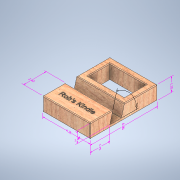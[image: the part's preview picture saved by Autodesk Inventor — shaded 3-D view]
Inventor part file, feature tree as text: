
AUTODESK INVENTOR PART (.ipt)
format: ipt  version: 2020.2 (Build 242310000, 310)  size: 403,456 bytes
history: native  units: in
note: dims shown in document units (in); Inventor stores cm internally (conversion verified against a paired STEP export)
features: other x8, extrude x4, sketch x4, fillet x2
ambient origin geometry x8: Origin, YZ Plane, XZ Plane, XY Plane, X Axis, Y Axis, Z Axis, Center Point
bodies: Solid1 (feature_tree)
feature tree (18):
  other  "Annotations"
  extrude  "Extrusion1"  Depth=6.0in
  extrude  "Extrusion3"  Depth=1.25in
  extrude  "Extrusion4"  TaperAngle=75.0deg  [1 undecoded]
  extrude  "Extrusion5"  Depth=1.25in
  fillet  "Fillet1"  Radius=1.0in
  fillet  "Fillet2"  Radius=0.1in
  sketch  "Sketch2"  dims[d0=4.25in d1=6.0in]
  sketch  "Sketch4"  dims[d2=1.25in d3=0.0in d27=1.0in]
  sketch  "Sketch6"  dims[d28=1.75in d29=75.0deg]
  sketch  "Sketch7"  dims[d31=0.0in d32=0.0in d46=1.0in d50=1.0in d51=0.1in d52=0.0in d53=0.0625in d54=0.5in d55=0.5in d56=0.0in d57=0.0in d58=0.0625in d10=0.0949in d11=4.25in d12=0.3164in d13=0.1734in d14=6.0in d33=0.1905in d34=1.0in d35=0.2828in d36=0.1784in d37=1.25in d41=0.1884in d42=1.75in d43=0.314in d44=0.0802in d45=2.0179in d47=0.2389in d48=0.113in d49=75.0deg d9=0.1629in]
  other  "Linear Dimension 1"
  other  "Linear Dimension 2"
  other  "Linear Dimension 3"
  other  "Linear Dimension 4"
  other  "Linear Dimension 5"
  other  "Linear Dimension 6"
  other  "Angular Dimension 1"
note: 1 required parameter value undecoded (feature->parameter linkage not recoverable at this tier; creation-order binding heuristic only, values carry confidence <= 0.55)
